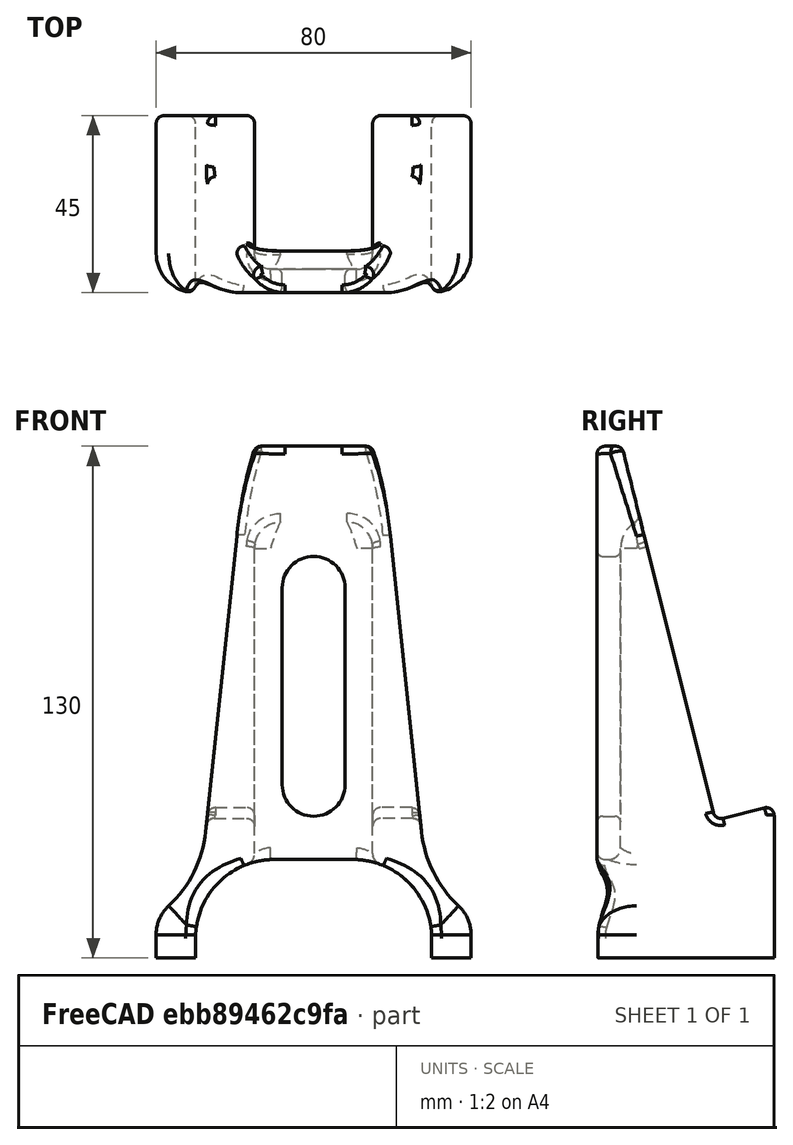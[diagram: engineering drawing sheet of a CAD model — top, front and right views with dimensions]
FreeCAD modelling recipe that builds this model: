
FCSTD DOCUMENT  (FreeCAD 1.0R38641 +678 (Git))
Label: IPhoneHolder
License: All rights reserved
LicenseURL: https://en.wikipedia.org/wiki/All_rights_reserved
objects: Part::Fillet×15, Part::Box×6, Part::MultiFuse×3, Part::Cut×2, Part::Chamfer×1, Part::Mirroring×1
note: 28 computed .brp shape members not serialized (recipe doc carries the construction recipe); baked Part::Feature solids carry a one-line shape summary decoded from their .brp

FEATURE [Part::Box] Box  label="Cube"
  AttacherType = Attacher::AttachEngine3D
  Height = 112
  Length = 30
  Placement = pos=(-15,6,0) rot=(0,0,1;0rad)
  Width = 60
FEATURE [Part::Fillet] Fillet
  Base = -> Box
  EdgeLinks = -> Box [Edge1,Edge5]
  Edges = 2 edges r=4: [Edge1,Edge5]
FEATURE [Part::Box] Box001  label="BaseBlock"
  AttacherType = Attacher::AttachEngine3D
  Height = 130
  Length = 40
  Placement = pos=(-40,0,0) rot=(-15,0,1;0rad)
  Width = 45
FEATURE [Part::Box] Box002  label="Cube002"
  AttacherType = Attacher::AttachEngine3D
  Height = 160
  Length = 50
  Placement = pos=(-80,0,10) rot=(0,1,0;0.10472rad)
  Width = 50
FEATURE [Part::Fillet] Fillet001
  Base = -> Fillet
  EdgeLinks = -> Fillet [Edge7]
  Edges = 1 edges r=8: [Edge7]
FEATURE [Part::Box] Box004  label="Cube004"
  AttacherType = Attacher::AttachEngine3D
  Height = 130
  Length = 30
  Placement = pos=(-30,30,35) rot=(1,0,0;0.244346rad)
  Width = 60
FEATURE [Part::Fillet] Fillet004
  Base = -> Box004
  EdgeLinks = -> Box004 [Edge9,Edge11]
  Edges = 2 edges r=2: [Edge9,Edge11]
FEATURE [Part::Box] Box005  label="Cube005"
  AttacherType = Attacher::AttachEngine3D
  Height = 30
  Length = 30
  Placement = pos=(-30,-5,-5) rot=(0,0,1;0rad)
  Width = 60
FEATURE [Part::Box] Box006  label="Cube006"
  AttacherType = Attacher::AttachEngine3D
  Height = 66
  Length = 10
  Placement = pos=(-8,-5,36) rot=(0,0,1;0rad)
  Width = 15
FEATURE [Part::Chamfer] Chamfer001
  Base = -> Box002
  EdgeLinks = -> Box002 [Edge8]
  Edges = 1 edges r=15: [Edge8]
FEATURE [Part::Fillet] Fillet017
  Base = -> Chamfer001
  EdgeLinks = -> Chamfer001 [Edge2]
  Edges = 1 edges r=30: [Edge2]
FEATURE [Part::MultiFuse] Fusion
  Shapes = -> [Fillet001,Fillet017]
FEATURE [Part::Cut] Cut
  Base = -> Box001
  Tool = -> Fusion
FEATURE [Part::Fillet] Fillet018
  Base = -> Cut
  EdgeLinks = -> Cut [?Edge2]
  Edges = 1 edges r=10: [Edge2]
FEATURE [Part::Fillet] Fillet019
  Base = -> Fillet018
  EdgeLinks = -> Fillet018 [Edge7]
  Edges = 1 edges r=10: [Edge7]
FEATURE [Part::Fillet] Fillet020
  Base = -> Box005
  EdgeLinks = -> Box005 [Edge2]
  Edges = 1 edges r=20: [Edge2]
FEATURE [Part::Fillet] Fillet021
  Base = -> Box006
  EdgeLinks = -> Box006 [Edge2,Edge4]
  Edges = 2 edges r=8: [Edge2,Edge4]
FEATURE [Part::MultiFuse] Fusion004
  Shapes = -> [Fillet020,Fillet021,Fillet004]
FEATURE [Part::Cut] Cut001
  Base = -> Fillet019
  Tool = -> Fusion004
FEATURE [Part::Fillet] Fillet022
  Base = -> Cut001
  EdgeLinks = -> Cut001 [Edge27]
  Edges = 1 edges r=3: [Edge27]
FEATURE [Part::Fillet] Fillet023
  Base = -> Fillet022
  EdgeLinks = -> Fillet022 [Edge56,Edge77]
  Edges = 2 edges r=1.5: [Edge56,Edge77]
FEATURE [Part::Fillet] Fillet024
  Base = -> Fillet023
  EdgeLinks = -> Fillet023 [Edge63]
  Edges = 1 edges r=2: [Edge63]
FEATURE [Part::Fillet] Fillet025
  Base = -> Fillet024
  EdgeLinks = -> Fillet024 [Edge17]
  Edges = 1 edges r=2: [Edge17]
FEATURE [Part::Fillet] Fillet026
  Base = -> Fillet025
  EdgeLinks = -> Fillet025 [Edge5]
  Edges = 1 edges r=2: [Edge5]
FEATURE [Part::Fillet] Fillet027
  Base = -> Fillet026
  EdgeLinks = -> Fillet026 [Edge106]
  Edges = 1 edges r=2: [Edge106]
FEATURE [Part::Fillet] Fillet028
  Base = -> Fillet027
  EdgeLinks = -> Fillet027 [Edge28]
  Edges = 1 edges r=2: [Edge28]
FEATURE [Part::Mirroring] Part__Mirroring  label="Fillet028 (Mirror #1)"
  Base = (0,0,0)
  Normal = (1,0,0)
  Source = -> Fillet028
FEATURE [Part::MultiFuse] Fusion005  label="Holder_V2"
  Shapes = -> [Fillet028,Part__Mirroring]
